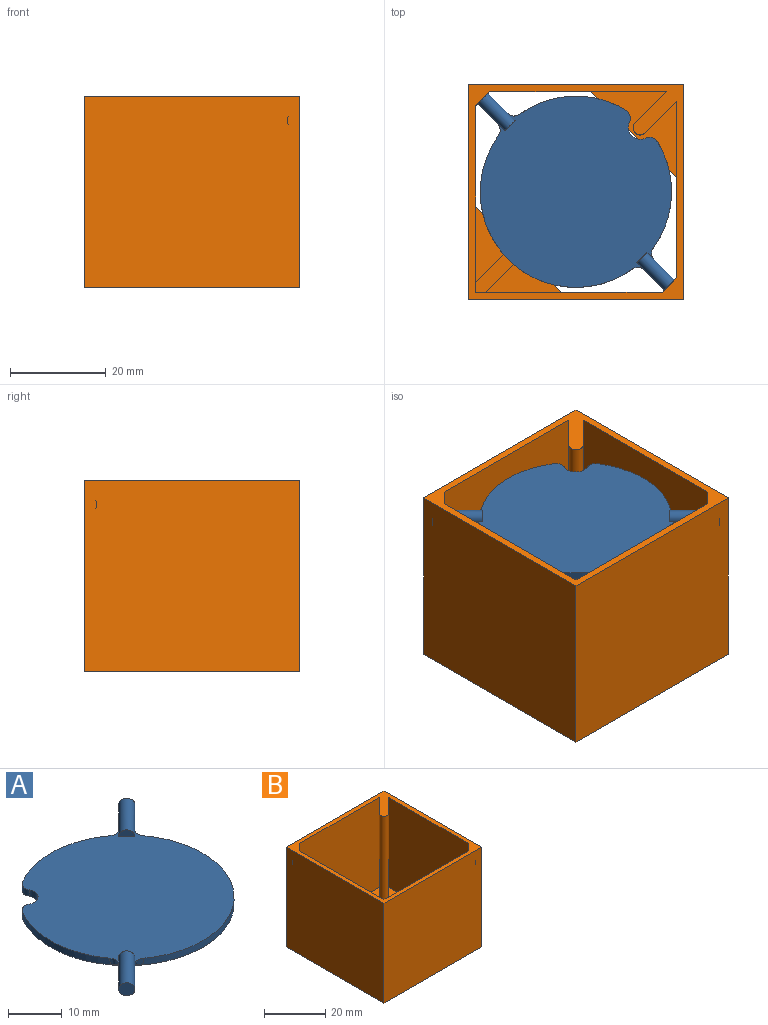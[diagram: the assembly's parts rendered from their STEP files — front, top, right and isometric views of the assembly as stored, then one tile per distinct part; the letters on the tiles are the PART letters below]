
ASSEMBLY  parts=2 mates=1
PART A: 22 faces, bbox 44.2x44.2x3.5 mm
  f0: cylinder r=20mm len=31.96mm, axis (0,0,-1), area 85mm2, adj f2,f5,f17,f19
  f1: cylinder r=20mm len=22.38mm, axis (0,0,-1), area 35.3mm2, adj f2,f5,f7,f14
  f2: plane 40.05x40.05mm, normal (0,0,1), area 1239.9mm2, adj f0,f1,f3,f4,f6,f7,f8,f10
  f3: cylinder r=2.5mm len=3.57mm, axis (0,0,-1), area 9.2mm2, adj f2,f5,f6,f7
  f4: cylinder r=20mm len=22.38mm, axis (0,0,-1), area 35.3mm2, adj f2,f5,f6,f20
  f5: plane 40x40mm, normal (0,0,-1), area 1240.3mm2, adj f0,f1,f3,f4,f6,f7,f15,f16
  f6: cylinder r=2mm len=2.57mm, axis (0,0,1), area 4.4mm2, adj f2,f3,f4,f5
  f7: cylinder r=2mm len=2.57mm, axis (0,0,1), area 4.4mm2, adj f1,f2,f3,f5
  f8: cylinder r=1.5mm len=9.37mm, axis (0.71,0.71,0), area 88mm2, adj f2,f9,f10,f16,f17,f20,f21
  f9: plane 3x2.12mm, normal (-0.71,-0.71,0), area 7.1mm2, adj f8
  f10: plane 2.12x2.12mm, normal (0.71,0.71,0), area 3.5mm2, adj f2,f8
  f11: cylinder r=1.5mm len=9.37mm, axis (-0.71,-0.71,0), area 88mm2, adj f2,f12,f13,f14,f15,f18,f19
  f12: plane 3x2.12mm, normal (0.71,0.71,0), area 7.1mm2, adj f11
  f13: plane 2.12x2.12mm, normal (-0.71,-0.71,0), area 3.5mm2, adj f2,f11
  f14: bspline ~2.84x2.39mm, area 2.9mm2, adj f1,f2,f11,f15
  f15: bspline ~2.62x2.22mm, area 2.6mm2, adj f5,f11,f14
  f16: bspline ~2.62x2.22mm, area 2.6mm2, adj f5,f8,f17
  f17: bspline ~2.84x2.39mm, area 2.9mm2, adj f0,f2,f8,f16
  f18: bspline ~2.62x2.22mm, area 2.6mm2, adj f5,f11,f19
  f19: bspline ~2.84x2.39mm, area 2.9mm2, adj f0,f2,f11,f18
  f20: bspline ~2.84x2.39mm, area 2.9mm2, adj f2,f4,f8,f21
  f21: bspline ~2.62x2.22mm, area 2.6mm2, adj f5,f8,f20
PART B: 27 faces, bbox 45x45x40 mm
  f0: plane 40x36.88mm, normal (0,-1,0), area 1411.6mm2, adj f4,f10,f11,f22,f23,f24
  f1: plane 40x36.88mm, normal (-1,0,0), area 1411.6mm2, adj f5,f10,f11,f22,f23,f26
  f2: plane 40x39mm, normal (1,0,0), area 1432.8mm2, adj f3,f4,f10,f11,f16,f19,f20,f21
  f3: plane 40x39mm, normal (0,1,0), area 1432.8mm2, adj f2,f5,f10,f11,f16,f17,f20,f21
  f4: plane 40x3mm, normal (0.71,-0.71,0), area 159.5mm2, adj f0,f2,f10,f11,f14
  f5: plane 40x3mm, normal (-0.71,0.71,0), area 159.5mm2, adj f1,f3,f10,f11,f13
  f6: plane 45x40mm, normal (1,0,0), area 1800mm2, adj f7,f9,f10,f11
  f7: plane 45x40mm, normal (0,1,0), area 1800mm2, adj f6,f8,f10,f11
  f8: plane 45x40mm, normal (-1,0,0), area 1800mm2, adj f7,f9,f10,f11
  f9: plane 45x40mm, normal (0,-1,0), area 1800mm2, adj f6,f8,f10,f11
  f10: plane 45x45mm, normal (0,0,1), area 303.4mm2, adj f0,f1,f2,f3,f4,f5,f6,f7
  f11: plane 45x45mm, normal (0,0,-1), area 594mm2, adj f0,f1,f2,f3,f4,f5,f6,f7
  f12: plane 3.6x2.55mm, normal (-0.71,0.71,0), area 10.2mm2, adj f13
  f13: cylinder r=1.8mm len=4.26mm, axis (-0.71,0.71,0), area 27.4mm2, adj f5,f12
  f14: cylinder r=1.8mm len=4.26mm, axis (-0.71,0.71,0), area 27.4mm2, adj f4,f15
  f15: plane 3.6x2.55mm, normal (0.71,-0.71,0), area 10.2mm2, adj f14
  f16: plane 18x18mm, normal (0.71,0.71,0), area 101.8mm2, adj f2,f3,f11,f21
  f17: plane 26x6.5mm, normal (0.71,-0.71,0), area 239.2mm2, adj f3,f18,f20,f21
  f18: cylinder r=1.5mm len=26mm, axis (0,0,-1), area 122.5mm2, adj f17,f19,f20,f21
  f19: plane 26x6.5mm, normal (-0.71,0.71,0), area 239.2mm2, adj f2,f18,f20,f21
  f20: plane 9.07x9.07mm, normal (0,0,1), area 33.4mm2, adj f2,f3,f17,f18,f19
  f21: plane 18x18mm, normal (0,0,1), area 128.6mm2, adj f2,f3,f16,f17,f18,f19
  f22: plane 18x18mm, normal (-0.71,-0.71,0), area 101.8mm2, adj f0,f1,f11,f23
  f23: plane 18x18mm, normal (0,0,1), area 128.6mm2, adj f0,f1,f22,f24,f25,f26
  f24: plane 36x6.5mm, normal (-0.71,0.71,0), area 331.1mm2, adj f0,f10,f23,f25
  f25: cylinder r=1.5mm len=36mm, axis (0,0,-1), area 169.6mm2, adj f10,f23,f24,f26
  f26: plane 36x6.5mm, normal (0.71,-0.71,0), area 331.1mm2, adj f1,f10,f23,f25
PLACE A rot(axis=(0,0,-1),90deg) t=(-0.02,0.02,33.5)mm
PLACE B rot(axis=(0.89,0.31,-0.33),0deg) t=(0,0,0)mm fixed
MATE cylindrical A.f8 <-> B.f13  axis (-0.71,0.71,0) through (-21.06,21.06,35)mm
